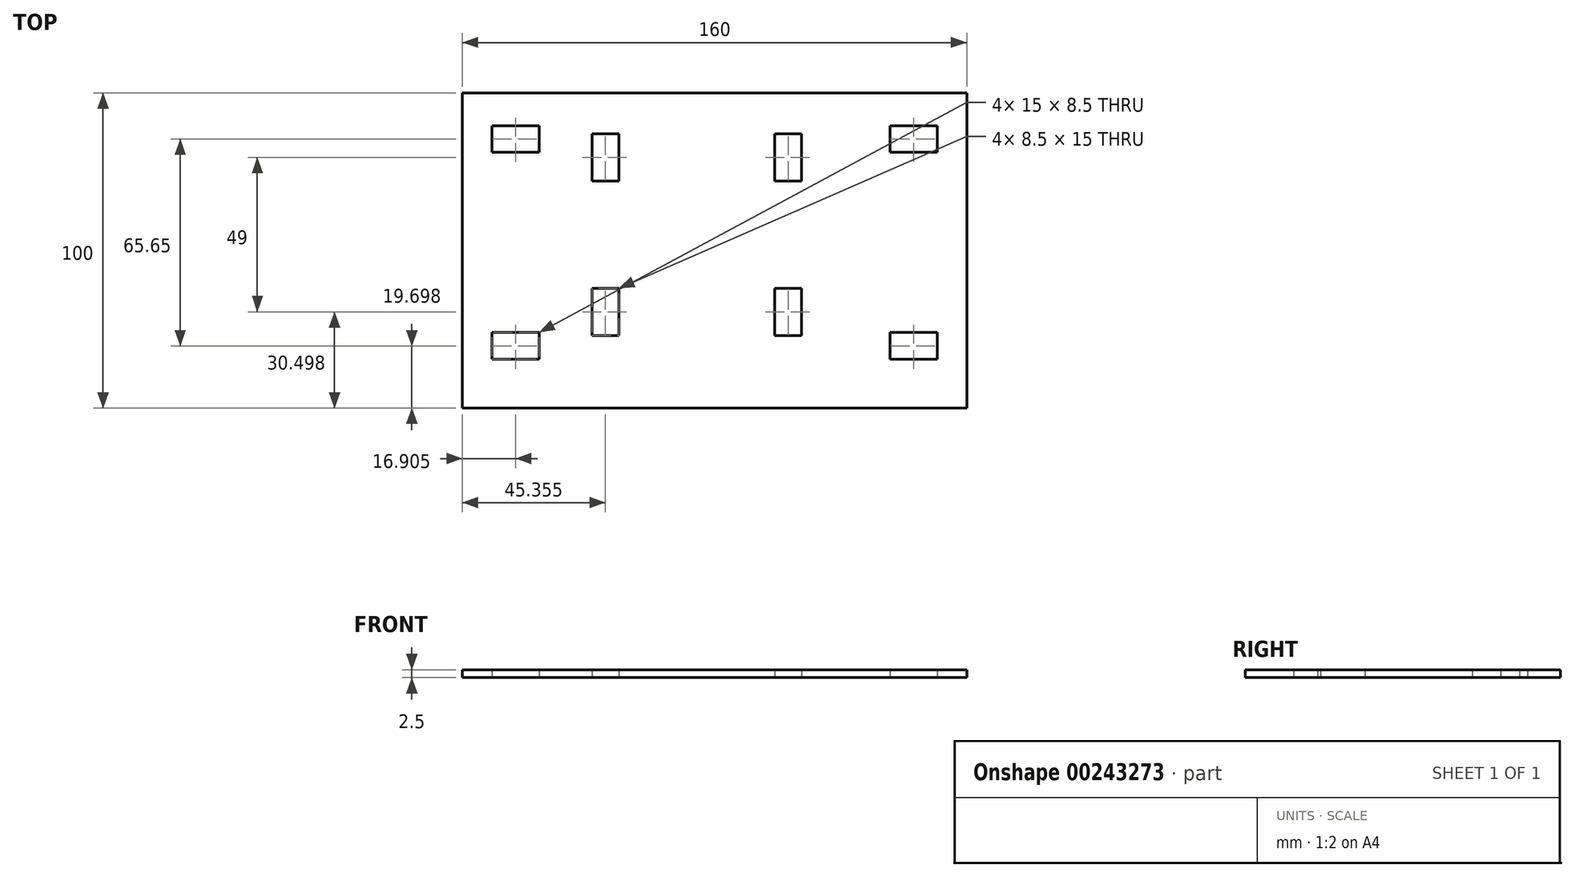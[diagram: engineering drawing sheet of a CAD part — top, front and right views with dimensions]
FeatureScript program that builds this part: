
annotation { "Feature Type Name" : "Feature", "Feature Type Description" : "" }
export const myFeature = defineFeature(function(context is Context, id is Id, definition is map)
    precondition{}
    {
        {
            var Q0;
            Q0=qCreatedBy(makeId("Top.planeOp"),FACE);
            var sketch = newSketch(context, id + "F0", { "sketchPlane" : qUnion([Q0])});
            skLineSegment(sketch, "E0.bottom", {"start": v(-622.9, -203.2) * mm, "end": v(-462.9, -203.2) * mm});
            skLineSegment(sketch, "E0.top", {"start": v(-622.9, -303.2) * mm, "end": v(-462.9, -303.2) * mm});
            skLineSegment(sketch, "E0.left", {"start": v(-622.9, -203.2) * mm, "end": v(-622.9, -303.2) * mm});
            skLineSegment(sketch, "E0.right", {"start": v(-462.9, -203.2) * mm, "end": v(-462.9, -303.2) * mm});
            skLineSegment(sketch, "E1.bottom", {"start": v(-598.5, -213.6) * mm, "end": v(-613.5, -213.6) * mm});
            skLineSegment(sketch, "E1.top", {"start": v(-598.5, -222.1) * mm, "end": v(-613.5, -222.1) * mm});
            skLineSegment(sketch, "E1.left", {"start": v(-598.5, -213.6) * mm, "end": v(-598.5, -222.1) * mm});
            skLineSegment(sketch, "E1.right", {"start": v(-613.5, -213.6) * mm, "end": v(-613.5, -222.1) * mm});
            skPoint(sketch, "E1.middle", {"position": v(-606, -217.85) * mm});
            skLineSegment(sketch, "E2.bottom", {"start": v(-581.8, -216.2) * mm, "end": v(-573.3, -216.2) * mm});
            skLineSegment(sketch, "E2.top", {"start": v(-581.8, -231.2) * mm, "end": v(-573.3, -231.2) * mm});
            skLineSegment(sketch, "E2.left", {"start": v(-581.8, -216.2) * mm, "end": v(-581.8, -231.2) * mm});
            skLineSegment(sketch, "E2.right", {"start": v(-573.3, -216.2) * mm, "end": v(-573.3, -231.2) * mm});
            skPoint(sketch, "E2.middle", {"position": v(-577.56, -223.7) * mm});
            skLineSegment(sketch, "E3.bottom", {"start": v(-523.8, -216.2) * mm, "end": v(-515.3, -216.2) * mm});
            skLineSegment(sketch, "E3.top", {"start": v(-523.8, -231.2) * mm, "end": v(-515.3, -231.2) * mm});
            skLineSegment(sketch, "E3.left", {"start": v(-523.8, -216.2) * mm, "end": v(-523.8, -231.2) * mm});
            skLineSegment(sketch, "E3.right", {"start": v(-515.3, -216.2) * mm, "end": v(-515.3, -231.2) * mm});
            skPoint(sketch, "E3.middle", {"position": v(-519.56, -223.7) * mm});
            skLineSegment(sketch, "E4.bottom", {"start": v(-581.8, -265.2) * mm, "end": v(-573.3, -265.2) * mm});
            skLineSegment(sketch, "E4.top", {"start": v(-581.8, -280.2) * mm, "end": v(-573.3, -280.2) * mm});
            skLineSegment(sketch, "E4.left", {"start": v(-581.8, -265.2) * mm, "end": v(-581.8, -280.2) * mm});
            skLineSegment(sketch, "E4.right", {"start": v(-573.3, -265.2) * mm, "end": v(-573.3, -280.2) * mm});
            skPoint(sketch, "E4.middle", {"position": v(-577.56, -272.7) * mm});
            skLineSegment(sketch, "E5.bottom", {"start": v(-523.8, -265.2) * mm, "end": v(-515.3, -265.2) * mm});
            skLineSegment(sketch, "E5.top", {"start": v(-523.8, -280.2) * mm, "end": v(-515.3, -280.2) * mm});
            skLineSegment(sketch, "E5.left", {"start": v(-523.8, -265.2) * mm, "end": v(-523.8, -280.2) * mm});
            skLineSegment(sketch, "E5.right", {"start": v(-515.3, -265.2) * mm, "end": v(-515.3, -280.2) * mm});
            skPoint(sketch, "E5.middle", {"position": v(-519.56, -272.7) * mm});
            skLineSegment(sketch, "E6.bottom", {"start": v(-598.5, -287.75) * mm, "end": v(-613.5, -287.75) * mm});
            skLineSegment(sketch, "E6.top", {"start": v(-598.5, -279.25) * mm, "end": v(-613.5, -279.25) * mm});
            skLineSegment(sketch, "E6.left", {"start": v(-598.5, -287.75) * mm, "end": v(-598.5, -279.25) * mm});
            skLineSegment(sketch, "E6.right", {"start": v(-613.5, -287.75) * mm, "end": v(-613.5, -279.25) * mm});
            skPoint(sketch, "E6.middle", {"position": v(-606, -283.5) * mm});
            skLineSegment(sketch, "E7.bottom", {"start": v(-472.3, -287.75) * mm, "end": v(-487.3, -287.75) * mm});
            skLineSegment(sketch, "E7.top", {"start": v(-472.3, -279.25) * mm, "end": v(-487.3, -279.25) * mm});
            skLineSegment(sketch, "E7.left", {"start": v(-472.3, -287.75) * mm, "end": v(-472.3, -279.25) * mm});
            skLineSegment(sketch, "E7.right", {"start": v(-487.3, -287.75) * mm, "end": v(-487.3, -279.25) * mm});
            skPoint(sketch, "E7.middle", {"position": v(-479.8, -283.5) * mm});
            skLineSegment(sketch, "E8.bottom", {"start": v(-472.3, -222.1) * mm, "end": v(-487.3, -222.1) * mm});
            skLineSegment(sketch, "E8.top", {"start": v(-472.3, -213.6) * mm, "end": v(-487.3, -213.6) * mm});
            skLineSegment(sketch, "E8.left", {"start": v(-472.3, -222.1) * mm, "end": v(-472.3, -213.6) * mm});
            skLineSegment(sketch, "E8.right", {"start": v(-487.3, -222.1) * mm, "end": v(-487.3, -213.6) * mm});
            skPoint(sketch, "E8.middle", {"position": v(-479.8, -217.85) * mm});
            skSolve(sketch);
        }
        {
            var Q0;
            Q0 = qSketchRegion(id + "F0", true);
            extrude(context, id + "F1", {"entities" : qUnion([Q0]), "depth" : 2.5 * mm});
        }
    });
